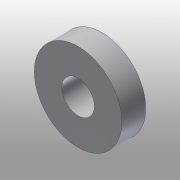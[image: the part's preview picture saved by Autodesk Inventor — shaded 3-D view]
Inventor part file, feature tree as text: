
AUTODESK INVENTOR PART (.ipt)
format: ipt  version: 2015 (Build 190159000, 159)  size: 83,968 bytes
history: native  units: mm
features: other x3, sketch x1
ambient origin geometry x8: Origin, YZ Plane, XZ Plane, XY Plane, X Axis, Y Axis, Z Axis, Center Point
bodies: Solid1 (feature_tree)
feature tree (4):
  other  "500-179.ipt"
  other  "Solid1::500-179.ipt"
  other  "TaggingFeature1"
  sketch  "Sketch1"  dims[d0=10.0mm]
